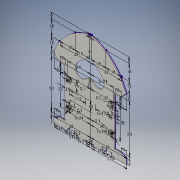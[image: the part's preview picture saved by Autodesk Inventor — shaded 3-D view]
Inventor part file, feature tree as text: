
AUTODESK INVENTOR PART (.ipt)
format: ipt  version: 2016 (Build 200138000, 138)  size: 406,016 bytes
history: native  units: mm
features: other x6, extrude x2, sketch x2, projected_geometry x1
ambient origin geometry x8: Origin, YZ Plane, XZ Plane, XY Plane, X Axis, Y Axis, Z Axis, Center Point
bodies: Body1 (feature_tree)
feature tree (11):
  other  "shitaita"
  other  "肉抜き"
  other  "作業平面1"
  other  "スペード"
  other  "作業平面3"
  extrude  "押し出し9"  Depth=50.0mm
  sketch  "スケッチ17"
  extrude  "押し出し10"  Depth=26.0mm
  sketch  "スケッチ13"
  projected_geometry  "投影ループ6"
  other  "イメージ9"
